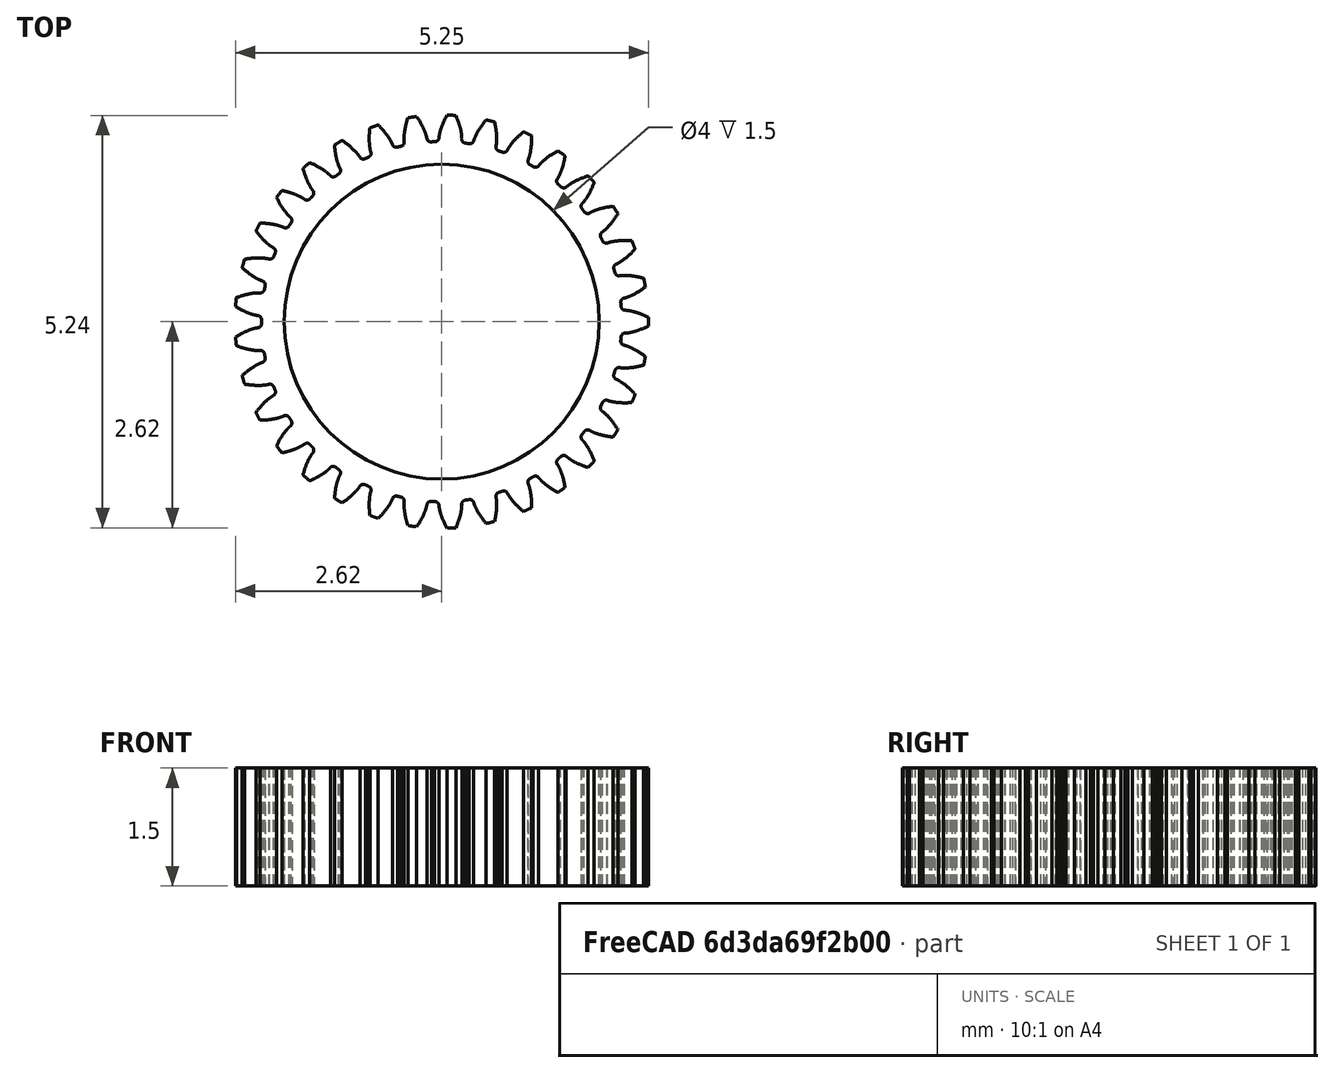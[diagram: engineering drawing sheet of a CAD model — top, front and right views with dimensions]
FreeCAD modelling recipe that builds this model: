
FCSTD DOCUMENT  (FreeCAD 0.18.1R)
Label: Pignion_M015_33
License: All rights reserved
LicenseURL: http://en.wikipedia.org/wiki/All_rights_reserved
objects: Part::Part2DObjectPython×1, PartDesign::Pad×1, Sketcher::SketchObject×1, PartDesign::Pocket×1, PartDesign::Body×1
note: 7 computed .brp shape members not serialized (recipe doc carries the construction recipe); baked Part::Feature solids carry a one-line shape summary decoded from their .brp

FEATURE [Part::Part2DObjectPython] InvoluteGear  # Draft 2D object (typed FeaturePython)
  ExternalGear = true
  HighPrecision = true
  Modules = 0.15
  NumberOfTeeth = 33
  PressureAngle = 20
FEATURE [PartDesign::Pad] Pad
  Length = 1.5
  Length2 = 100
  Profile = -> InvoluteGear
  Type = 0
FEATURE [Sketcher::SketchObject] Sketch
  MapMode = 2
  sketch-geometry (1):
    g0: Circle CenterX=0 CenterY=0 CenterZ=0 NormalX=0 NormalY=0 NormalZ=1 AngleXU=0 Radius=2
  constraints (2):
    c: Coincident(g0,g-1)
    c: Radius(g0) = 2
FEATURE [PartDesign::Pocket] Pocket
  BaseFeature = -> Pad
  Length = 5
  Length2 = 100
  Profile = -> Sketch
  Reversed = true
  Type = 1
FEATURE [PartDesign::Body] Body
  Group = -> [InvoluteGear,Pad,Sketch,Pocket]
  Origin = -> Origin
  Tip = -> Pocket
